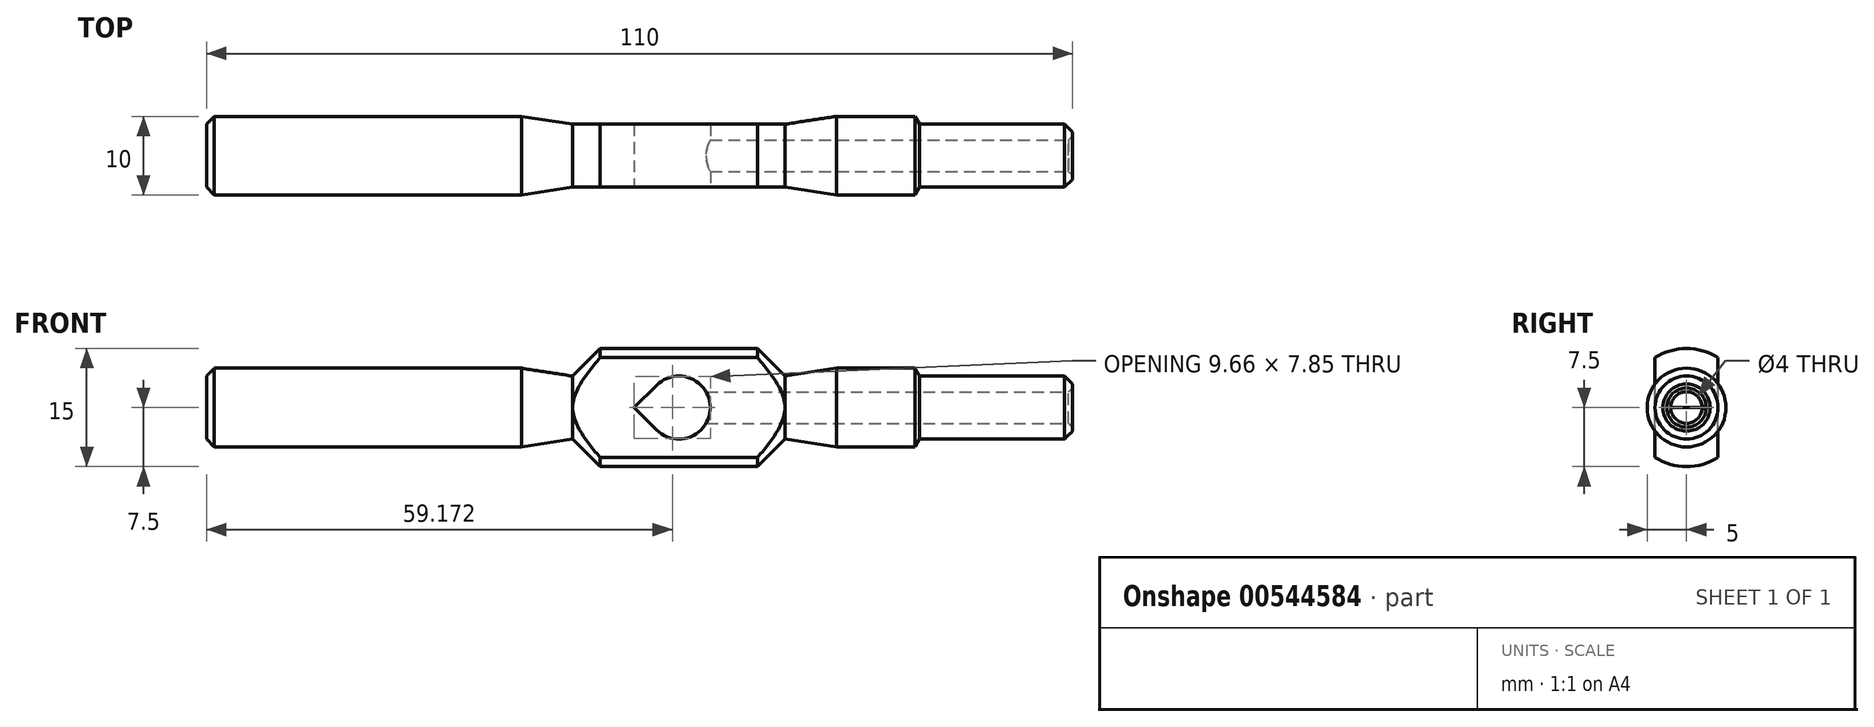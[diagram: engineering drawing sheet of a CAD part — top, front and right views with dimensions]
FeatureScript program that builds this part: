
annotation { "Feature Type Name" : "Feature", "Feature Type Description" : "" }
export const myFeature = defineFeature(function(context is Context, id is Id, definition is map)
    precondition{}
    {
        {
            var Q0;
            Q0=qCreatedBy(makeId("Top.planeOp"),FACE);
            var sketch = newSketch(context, id + "F0", { "sketchPlane" : qUnion([Q0])});
            skLineSegment(sketch, "E0", {"start": v(30, 5) * mm, "end": v(20, 5) * mm});
            skLineSegment(sketch, "E1", {"start": v(20, 5) * mm, "end": v(13.5, 4) * mm});
            skLineSegment(sketch, "E2", {"start": v(13.5, 4) * mm, "end": v(10, 7.5) * mm});
            skLineSegment(sketch, "E3", {"start": v(10, 7.5) * mm, "end": v(0, 7.5) * mm});
            skLineSegment(sketch, "E4", {"start": v(50, 0) * mm, "end": v(0, 0) * mm});
            skLineSegment(sketch, "E5", {"start": v(0, -21.6) * mm, "end": v(0, 28.17) * mm, "construction": true});
            skLineSegment(sketch, "E6.MirrorCS", {"start": v(-20, 5) * mm, "end": v(-13.5, 4) * mm});
            skLineSegment(sketch, "E7.MirrorCS", {"start": v(-13.5, 4) * mm, "end": v(-10, 7.5) * mm});
            skLineSegment(sketch, "E8.MirrorCS", {"start": v(-60, 5) * mm, "end": v(-20, 5) * mm});
            skLineSegment(sketch, "E9.MirrorCS", {"start": v(-60, 0) * mm, "end": v(-60, 5) * mm});
            skLineSegment(sketch, "E10.MirrorCS", {"start": v(-60, 0) * mm, "end": v(0, 0) * mm});
            skLineSegment(sketch, "E11.MirrorCS", {"start": v(-10, 7.5) * mm, "end": v(0, 7.5) * mm});
            skLineSegment(sketch, "E12", {"start": v(30, 5) * mm, "end": v(30.58, 4) * mm});
            skLineSegment(sketch, "E13", {"start": v(30.58, 4) * mm, "end": v(50, 4) * mm});
            skLineSegment(sketch, "E14", {"start": v(50, 4) * mm, "end": v(50, 0) * mm});
            skSolve(sketch);
        }
        {
            var Q0;
            Q0=makeQuery(id+"F0.imprint","IMPRINT",FACE,{"disambiguationData":[TD([[makeQuery(id+"F0.imprint","IMPRINT",EDGE,{"derivedFrom":sQuery(id+"F0.wireOp",EDGE,"E0")}),1.0]])]});
            var Q1;
            Q1=sQuery(id+"F0.wireOp",EDGE,"E10.MirrorCS");
            revolve(context, id + "F1", {"entities" : qUnion([Q0]), "axis" : qUnion([Q1]), "revolveType" : RevolveType.FULL});
        }
        {
            var Q0;
            Q0=qCreatedBy(makeId("Top.planeOp"),FACE);
            var sketch = newSketch(context, id + "F2", { "sketchPlane" : qUnion([Q0])});
            skLineSegment(sketch, "E15.bottom", {"start": v(-13.5, 14.54) * mm, "end": v(13.5, 14.54) * mm});
            skLineSegment(sketch, "E15.top", {"start": v(-13.5, 4) * mm, "end": v(13.5, 4) * mm});
            skLineSegment(sketch, "E15.left", {"start": v(-13.5, 14.54) * mm, "end": v(-13.5, 4) * mm});
            skLineSegment(sketch, "E15.right", {"start": v(13.5, 14.54) * mm, "end": v(13.5, 4) * mm});
            skLineSegment(sketch, "E16", {"start": v(-17.92, 0) * mm, "end": v(20.11, 0) * mm, "construction": true});
            skLineSegment(sketch, "E17.MirrorCS", {"start": v(-13.5, -14.54) * mm, "end": v(-13.5, -4) * mm});
            skLineSegment(sketch, "E18.MirrorCS", {"start": v(-13.5, -14.54) * mm, "end": v(13.5, -14.54) * mm});
            skLineSegment(sketch, "E19.MirrorCS", {"start": v(13.5, -14.54) * mm, "end": v(13.5, -4) * mm});
            skLineSegment(sketch, "E20.MirrorCS", {"start": v(-13.5, -4) * mm, "end": v(13.5, -4) * mm});
            skSolve(sketch);
        }
        {
            var Q0;
            Q0=makeQuery(id+"F2.imprint","IMPRINT",FACE,{"disambiguationData":[TD([[makeQuery(id+"F2.imprint","IMPRINT",EDGE,{"derivedFrom":sQuery(id+"F2.wireOp",EDGE,"E15.bottom")}),-1.0]])]});
            var Q1;
            Q1=makeQuery(id+"F2.imprint","IMPRINT",FACE,{"disambiguationData":[TD([[makeQuery(id+"F2.imprint","IMPRINT",EDGE,{"derivedFrom":sQuery(id+"F2.wireOp",EDGE,"E17.MirrorCS")}),-1.0]])]});
            extrude(context, id + "F3", {"entities" : qUnion([Q0, Q1]), "operationType" : NewBodyOperationType.REMOVE, "endBound" : BoundingType.SYMMETRIC, "oppositeDirection" : true, "depth" : 25 * mm, "offsetDistance" : 25 * mm});
        }
        {
            var Q0;
            Q0=makeQuery(id+"F1.opRevolve","SWEPT_EDGE",EDGE,{"disambiguationData":[OSD([sQuery(id+"F0.wireOp",EDGE,"E8.MirrorCS"),sQuery(id+"F0.wireOp",EDGE,"E9.MirrorCS")])]});
            var Q1;
            Q1=makeQuery(id+"F1.opRevolve","SWEPT_EDGE",EDGE,{"disambiguationData":[OSD([sQuery(id+"F0.wireOp",EDGE,"E13"),sQuery(id+"F0.wireOp",EDGE,"E14")])]});
            chamfer(context, id + "F4", {"entities" : qUnion([Q0, Q1]), "width" : 1 * mm, "tangentPropagation" : true});
        }
        {
            var Q0;
            Q0=makeQuery(id+"F3.boolean.opBoolean","COPY",FACE,{"derivedFrom":makeQuery(id+"F3.opExtrude","SWEPT_FACE",FACE,{"disambiguationData":[OSD([sQuery(id+"F2.wireOp",EDGE,"E20.MirrorCS")])]})});
            var sketch = newSketch(context, id + "F5", { "sketchPlane" : qUnion([Q0])});
            skCircle(sketch, "E21", {"center": v(0, 0) * mm, "radius": 4 * mm});
            skLineSegment(sketch, "E22", {"start": v(-2.83, 2.83) * mm, "end": v(-5.66, 0) * mm});
            skLineSegment(sketch, "E23", {"start": v(-5.66, 0) * mm, "end": v(-2.83, -2.83) * mm});
            skSolve(sketch);
        }
        {
            var Q0;
            {var subQ0=sQuery(id+"F5.wireOp",EDGE,"E21");var subQ1=makeQuery(id+"F5.imprint","INTERSECT",VERTEX,{"derivedFrom":[subQ0,sQuery(id+"F5.wireOp",EDGE,"E22")]});Q0=makeQuery(id+"F5.imprint","IMPRINT",FACE,{"disambiguationData":[TD([[makeQuery(id+"F5.imprint","IMPRINT",EDGE,{"disambiguationData":[TD([[subQ1,-1.0]])],"derivedFrom":subQ0}),1.0]])]});}
            var Q1;
            {var subQ0=sQuery(id+"F5.wireOp",EDGE,"E22");Q1=makeQuery(id+"F5.imprint","IMPRINT",FACE,{"disambiguationData":[TD([[makeQuery(id+"F5.imprint","IMPRINT",EDGE,{"derivedFrom":subQ0}),1.0]])]});}
            extrude(context, id + "F6", {"entities" : qUnion([Q0, Q1]), "operationType" : NewBodyOperationType.REMOVE, "endBound" : BoundingType.SYMMETRIC, "oppositeDirection" : true, "depth" : 25 * mm, "offsetDistance" : 25 * mm});
        }
        {
            var Q0;
            Q0=makeQuery(id+"F1.opRevolve","SWEPT_FACE",FACE,{"disambiguationData":[OSD([sQuery(id+"F0.wireOp",EDGE,"E14")])]});
            var sketch = newSketch(context, id + "F7", { "sketchPlane" : qUnion([Q0])});
            skPoint(sketch, "E24", {"position": v(0, 0) * mm});
            skSolve(sketch);
        }
        {
            var Q0;
            Q0=sQuery(id+"F7.wireOp",VERTEX,"E24");
            var Q1;
            Q1=makeQuery(id+"F1.opRevolve","SWEPT_BODY",BODY,{"disambiguationData":[OSD([sQuery(id+"F0.wireOp",EDGE,"pWswsGux-O0Ji-8klV-9gw3-PypMn1qCg1gj"),sQuery(id+"F0.wireOp",EDGE,"E0"),sQuery(id+"F0.wireOp",EDGE,"E1"),sQuery(id+"F0.wireOp",EDGE,"E2"),sQuery(id+"F0.wireOp",EDGE,"E3"),sQuery(id+"F0.wireOp",EDGE,"E4"),sQuery(id+"F0.wireOp",EDGE,"E6.MirrorCS"),sQuery(id+"F0.wireOp",EDGE,"E7.MirrorCS"),sQuery(id+"F0.wireOp",EDGE,"E8.MirrorCS"),sQuery(id+"F0.wireOp",EDGE,"E9.MirrorCS"),sQuery(id+"F0.wireOp",EDGE,"E10.MirrorCS"),sQuery(id+"F0.wireOp",EDGE,"E11.MirrorCS")])]});
            hole(context, id + "F8", {"style" : HoleStyle.C_SINK, "endStyle" : HoleEndStyle.BLIND, "holeDiameter" : 4 * mm, "cSinkDiameter" : 5 * mm, "cSinkAngle" : 90 * degree, "holeDepth" : 50 * mm, "isTappedThrough" : true, "tappedDepth" : 5 * mm, "tapClearance" : 3, "locations" : qUnion([Q0]), "scope" : qUnion([Q1])});
        }
    });
